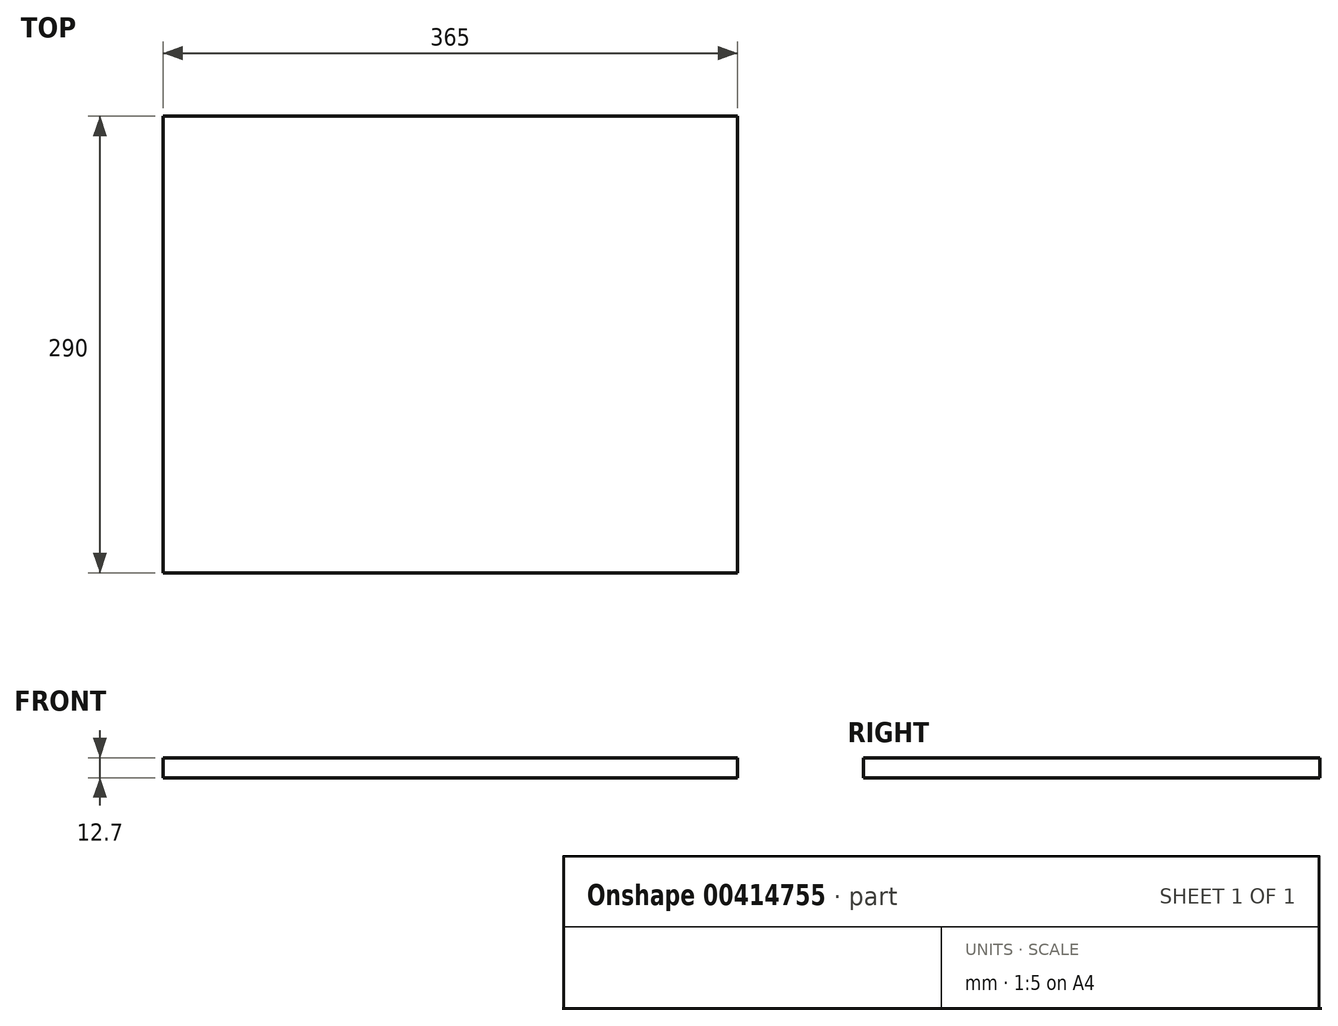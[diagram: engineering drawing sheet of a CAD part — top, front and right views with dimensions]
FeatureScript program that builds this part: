
annotation { "Feature Type Name" : "Feature", "Feature Type Description" : "" }
export const myFeature = defineFeature(function(context is Context, id is Id, definition is map)
    precondition{}
    {
        {
            var Q0;
            Q0=qCreatedBy(makeId("Top.planeOp"),FACE);
            var sketch = newSketch(context, id + "F0", { "sketchPlane" : qUnion([Q0])});
            skLineSegment(sketch, "E0.bottom", {"start": v(-70.96, 65.05) * mm, "end": v(294.04, 65.05) * mm});
            skLineSegment(sketch, "E0.top", {"start": v(-70.96, -224.95) * mm, "end": v(294.04, -224.95) * mm});
            skLineSegment(sketch, "E0.left", {"start": v(-70.96, 65.05) * mm, "end": v(-70.96, -224.95) * mm});
            skLineSegment(sketch, "E0.right", {"start": v(294.04, 65.05) * mm, "end": v(294.04, -224.95) * mm});
            skSolve(sketch);
        }
        {
            var Q0;
            Q0=qSketchRegion(id+"F0",true);
            extrude(context, id + "F1", {"entities" : qUnion([Q0]), "depth" : 12.7 * mm});
        }
    });
